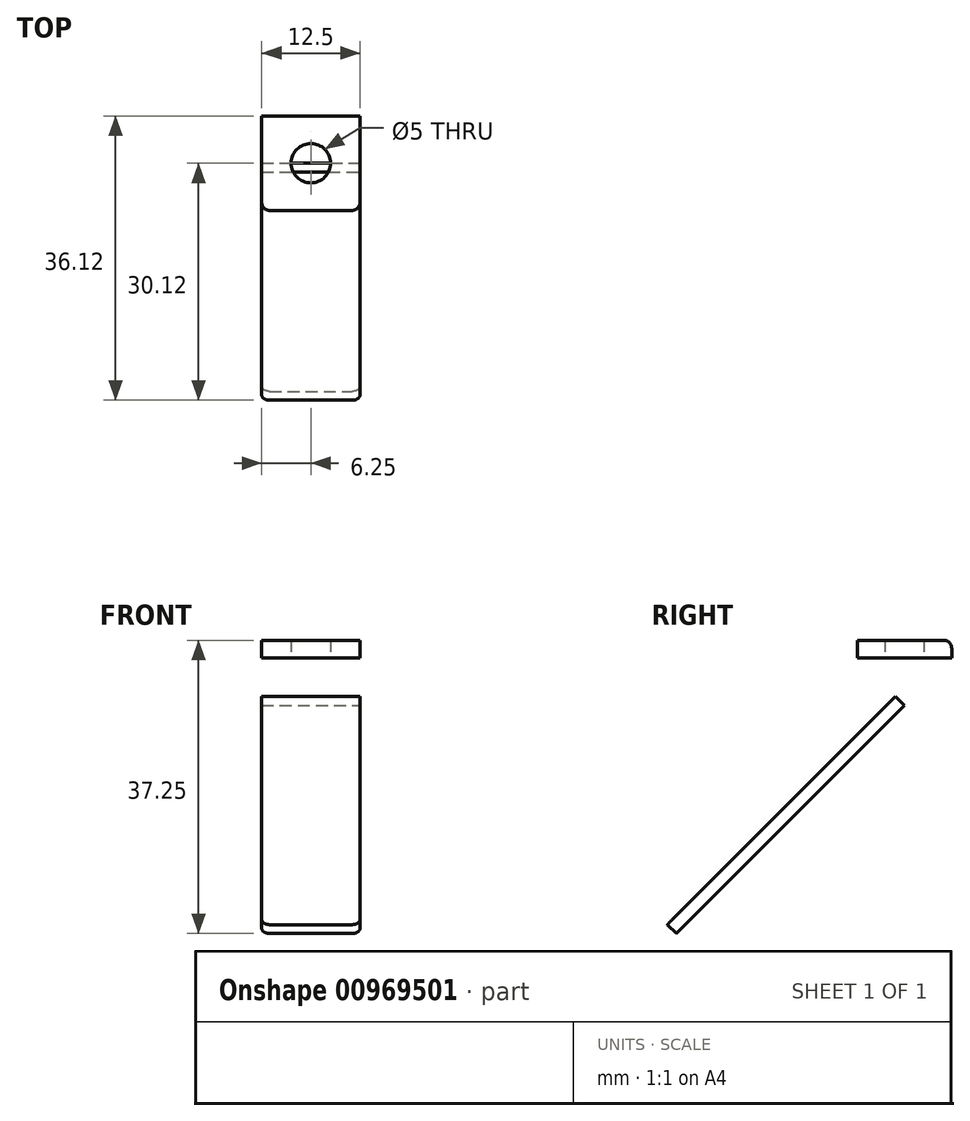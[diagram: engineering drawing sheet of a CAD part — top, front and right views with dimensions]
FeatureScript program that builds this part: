
annotation { "Feature Type Name" : "Feature", "Feature Type Description" : "" }
export const myFeature = defineFeature(function(context is Context, id is Id, definition is map)
    precondition{}
    {
        {
            var Q0;
            Q0=qCreatedBy(makeId("Top.planeOp"),FACE);
            var sketch = newSketch(context, id + "F0", { "sketchPlane" : qUnion([Q0])});
            skLineSegment(sketch, "E0.bottom", {"start": v(-6.25, 6) * mm, "end": v(6.25, 6) * mm});
            skLineSegment(sketch, "E0.top", {"start": v(-6.25, -6) * mm, "end": v(6.25, -6) * mm});
            skLineSegment(sketch, "E0.left", {"start": v(-6.25, 6) * mm, "end": v(-6.25, -6) * mm});
            skLineSegment(sketch, "E0.right", {"start": v(6.25, 6) * mm, "end": v(6.25, -6) * mm});
            skPoint(sketch, "E0.middle", {"position": v(0, 0) * mm});
            skCircle(sketch, "E1", {"center": v(0, 0) * mm, "radius": 2.5 * mm});
            skSolve(sketch);
        }
        {
            var Q0;
            Q0=makeQuery(id+"F0.imprint","IMPRINT",FACE,{"disambiguationData":[TD([[makeQuery(id+"F0.imprint","IMPRINT",EDGE,{"derivedFrom":sQuery(id+"F0.wireOp",EDGE,"E0.bottom")}),-1.0]])]});
            extrude(context, id + "F1", {"entities" : qUnion([Q0]), "depth" : 2.25 * mm, "offsetDistance" : 25 * mm});
        }
        {
            var Q0;
            Q0=makeQuery(id+"F1.opExtrude","CAP_FACE",FACE,{"disambiguationData":[OSD([sQuery(id+"F0.wireOp",EDGE,"E0.bottom"),sQuery(id+"F0.wireOp",EDGE,"E0.top"),sQuery(id+"F0.wireOp",EDGE,"E0.left"),sQuery(id+"F0.wireOp",EDGE,"E0.right"),sQuery(id+"F0.wireOp",EDGE,"E1")])],"isStart":false});
            var Q1;
            Q1=makeQuery(id+"F1.opExtrude","CAP_EDGE",EDGE,{"disambiguationData":[OSD([sQuery(id+"F0.wireOp",EDGE,"E0.bottom")])],"isStart":false});
            cPlane(context, id + "F2", {"entities" : qUnion([Q0, Q1]), "cplaneType" : CPlaneType.LINE_ANGLE, "offset" : 25 * mm, "angle" : 45 * degree, "width" : 150 * mm, "height" : 150 * mm});
        }
        {
            var Q0;
            Q0=qCreatedBy(id+"F2.planeOp",FACE);
            var sketch = newSketch(context, id + "F3", { "sketchPlane" : qUnion([Q0])});
            skLineSegment(sketch, "E2.bottom", {"start": v(6.25, -4.24) * mm, "end": v(-6.25, -4.24) * mm});
            skLineSegment(sketch, "E2.top", {"start": v(6.25, -45.24) * mm, "end": v(-6.25, -45.24) * mm});
            skLineSegment(sketch, "E2.left", {"start": v(6.25, -4.24) * mm, "end": v(6.25, -45.24) * mm});
            skLineSegment(sketch, "E2.right", {"start": v(-6.25, -4.24) * mm, "end": v(-6.25, -45.24) * mm});
            skSolve(sketch);
        }
        {
            var Q0;
            Q0=makeQuery(id+"F3.imprint","IMPRINT",FACE,{"disambiguationData":[TD([[makeQuery(id+"F3.imprint","IMPRINT",EDGE,{"derivedFrom":sQuery(id+"F3.wireOp",EDGE,"E2.bottom")}),1.0]])]});
            extrude(context, id + "F4", {"entities" : qUnion([Q0]), "operationType" : NewBodyOperationType.ADD, "depth" : 1.6 * mm, "offsetDistance" : 25 * mm});
        }
        {
            var Q0;
            Q0=makeQuery(id+"F1.opExtrude","SWEPT_EDGE",EDGE,{"disambiguationData":[OSD([sQuery(id+"F0.wireOp",EDGE,"E0.top"),sQuery(id+"F0.wireOp",EDGE,"E0.left")])]});
            var Q1;
            Q1=makeQuery(id+"F1.opExtrude","SWEPT_EDGE",EDGE,{"disambiguationData":[OSD([sQuery(id+"F0.wireOp",EDGE,"E0.top"),sQuery(id+"F0.wireOp",EDGE,"E0.right")])]});
            var Q2;
            Q2=makeQuery(id+"F4.opExtrude","SWEPT_EDGE",EDGE,{"disambiguationData":[OSD([sQuery(id+"F3.wireOp",EDGE,"E2.top"),sQuery(id+"F3.wireOp",EDGE,"E2.left")])]});
            var Q3;
            Q3=makeQuery(id+"F4.opExtrude","SWEPT_EDGE",EDGE,{"disambiguationData":[OSD([sQuery(id+"F3.wireOp",EDGE,"E2.top"),sQuery(id+"F3.wireOp",EDGE,"E2.right")])]});
            var Q4;
            Q4=makeQuery(id+"F1.opExtrude","CAP_EDGE",EDGE,{"disambiguationData":[OSD([sQuery(id+"F0.wireOp",EDGE,"E0.bottom")])],"isStart":false});
            fillet(context, id + "F5", {"entities" : qUnion([Q0, Q1, Q2, Q3, Q4]), "radius" : 1 * mm, "tangentPropagation" : true, "allowEdgeOverflow" : false});
        }
    });
